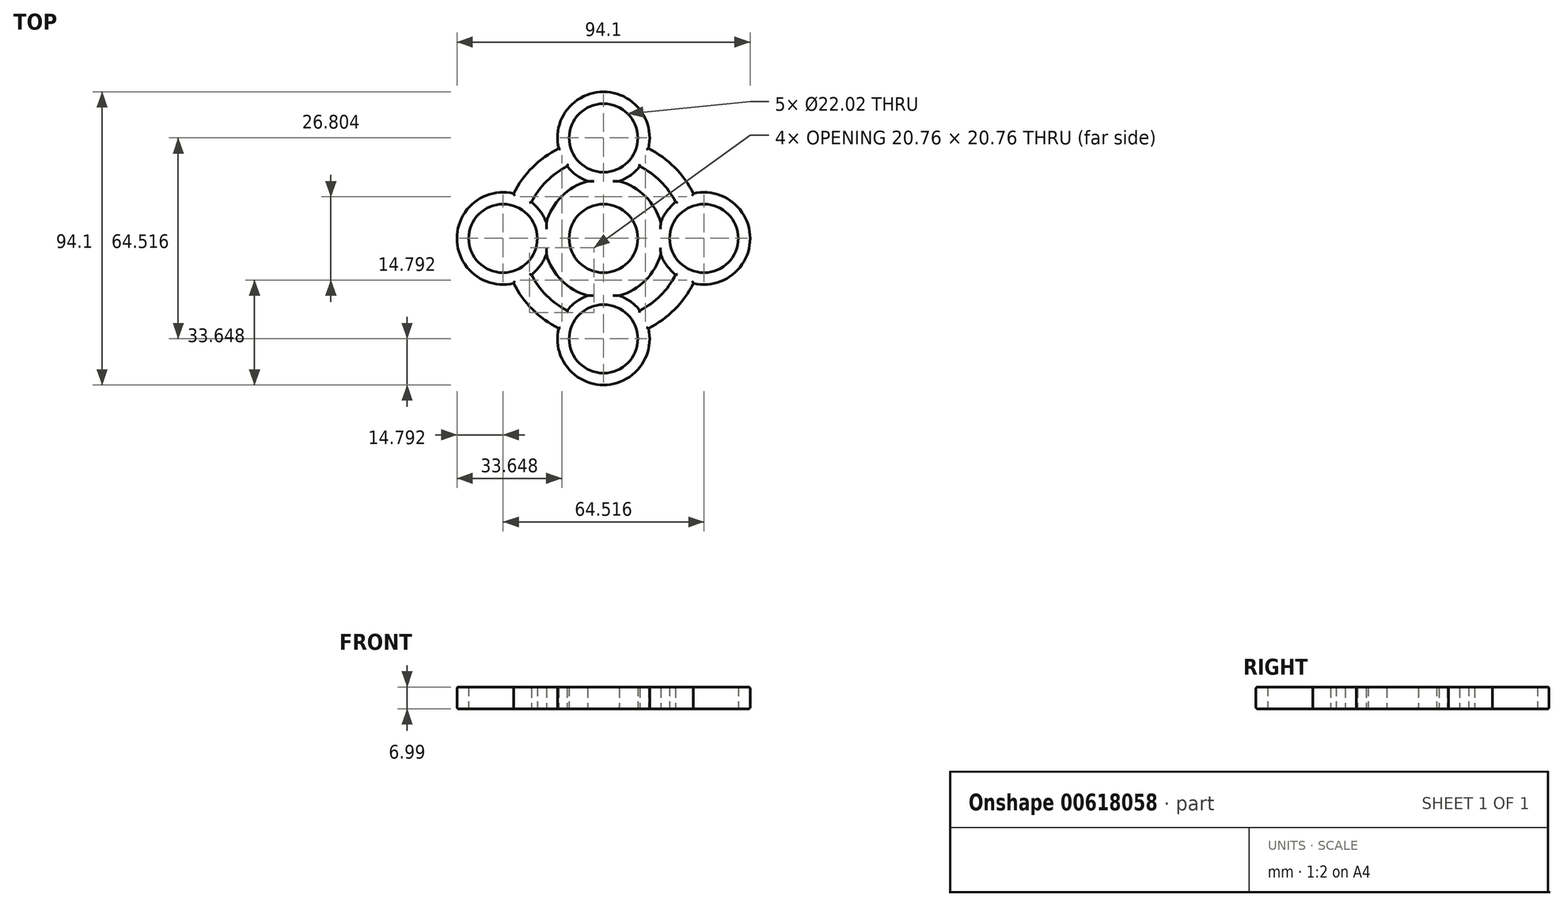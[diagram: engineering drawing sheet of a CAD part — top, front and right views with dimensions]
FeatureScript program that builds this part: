
annotation { "Feature Type Name" : "Feature", "Feature Type Description" : "" }
export const myFeature = defineFeature(function(context is Context, id is Id, definition is map)
    precondition{}
    {
        {
            var Q0;
            Q0=qCreatedBy(makeId("Top.planeOp"),FACE);
            var sketch = newSketch(context, id + "F0", { "sketchPlane" : qUnion([Q0])});
            skCircle(sketch, "E0", {"center": v(0, 0) * mm, "radius": 11.01 * mm});
            skCircle(sketch, "E1", {"center": v(-32.26, 0) * mm, "radius": 11.01 * mm});
            skCircle(sketch, "E2", {"center": v(0, 32.26) * mm, "radius": 11.01 * mm});
            skCircle(sketch, "E3", {"center": v(0, -32.26) * mm, "radius": 11.01 * mm});
            skCircle(sketch, "E4", {"center": v(32.26, 0) * mm, "radius": 11.01 * mm});
            skCircle(sketch, "E5", {"center": v(0, 32.26) * mm, "radius": 14.8 * mm});
            skCircle(sketch, "E6", {"center": v(-32.26, 0) * mm, "radius": 14.8 * mm});
            skCircle(sketch, "E7", {"center": v(0, -32.26) * mm, "radius": 14.8 * mm});
            skCircle(sketch, "E8", {"center": v(32.26, 0) * mm, "radius": 14.8 * mm});
            skLineSegment(sketch, "E9", {"start": v(-32.26, 0) * mm, "end": v(0, 0) * mm});
            skLineSegment(sketch, "E10", {"start": v(0, 0) * mm, "end": v(0, 32.26) * mm});
            skLineSegment(sketch, "E11", {"start": v(32.26, 0) * mm, "end": v(0, 0) * mm});
            skLineSegment(sketch, "E12", {"start": v(0, 0) * mm, "end": v(0, -32.26) * mm});
            skArc(sketch, "E13", {"start": v(-28.86, -14.4) * mm, "mid": v(-22.8, -22.8) * mm, "end": v(-14.4, -28.86) * mm});
            skArc(sketch, "E14.trimOffspring", {"start": v(-14.4, 28.86) * mm, "mid": v(-22.8, 22.8) * mm, "end": v(-28.86, 14.4) * mm});
            skArc(sketch, "E15.trimOffspring", {"start": v(28.86, 14.4) * mm, "mid": v(22.8, 22.8) * mm, "end": v(14.4, 28.86) * mm});
            skArc(sketch, "E16.trimOffspring", {"start": v(14.4, -28.86) * mm, "mid": v(22.8, -22.8) * mm, "end": v(28.86, -14.4) * mm});
            skArc(sketch, "E17", {"start": v(-23.14, -11.65) * mm, "mid": v(-18.32, -18.32) * mm, "end": v(-11.65, -23.14) * mm});
            skArc(sketch, "E18.trimOffspring", {"start": v(-11.65, 23.14) * mm, "mid": v(-18.32, 18.32) * mm, "end": v(-23.14, 11.65) * mm});
            skArc(sketch, "E19.trimOffspring", {"start": v(23.14, 11.65) * mm, "mid": v(18.32, 18.32) * mm, "end": v(11.65, 23.14) * mm});
            skArc(sketch, "E20.trimOffspring", {"start": v(11.65, -23.14) * mm, "mid": v(18.32, -18.32) * mm, "end": v(23.14, -11.65) * mm});
            skCircle(sketch, "E21", {"center": v(0, 0) * mm, "radius": 19.05 * mm});
            skSolve(sketch);
        }
        {
            var Q0;
            {var subQ0=sQuery(id+"F0.wireOp",EDGE,"E14.trimOffspring");Q0=makeQuery(id+"F0.imprint","IMPRINT",FACE,{"disambiguationData":[TD([[makeQuery(id+"F0.imprint","IMPRINT",EDGE,{"derivedFrom":subQ0}),1.0]])]});}
            var Q1;
            Q1=makeQuery(id+"F0.imprint","IMPRINT",FACE,{"disambiguationData":[TD([[makeQuery(id+"F0.imprint","IMPRINT",EDGE,{"derivedFrom":sQuery(id+"F0.wireOp",EDGE,"E1")}),-1.0]])]});
            var Q2;
            Q2=makeQuery(id+"F0.imprint","IMPRINT",FACE,{"disambiguationData":[TD([[makeQuery(id+"F0.imprint","IMPRINT",EDGE,{"derivedFrom":sQuery(id+"F0.wireOp",EDGE,"E2")}),-1.0]])]});
            var Q3;
            {var subQ0=sQuery(id+"F0.wireOp",EDGE,"E15.trimOffspring");Q3=makeQuery(id+"F0.imprint","IMPRINT",FACE,{"disambiguationData":[TD([[makeQuery(id+"F0.imprint","IMPRINT",EDGE,{"derivedFrom":subQ0}),1.0]])]});}
            var Q4;
            Q4=makeQuery(id+"F0.imprint","IMPRINT",FACE,{"disambiguationData":[TD([[makeQuery(id+"F0.imprint","IMPRINT",EDGE,{"derivedFrom":sQuery(id+"F0.wireOp",EDGE,"E4")}),-1.0]])]});
            var Q5;
            {var subQ0=sQuery(id+"F0.wireOp",EDGE,"E16.trimOffspring");Q5=makeQuery(id+"F0.imprint","IMPRINT",FACE,{"disambiguationData":[TD([[makeQuery(id+"F0.imprint","IMPRINT",EDGE,{"derivedFrom":subQ0}),1.0]])]});}
            var Q6;
            Q6=makeQuery(id+"F0.imprint","IMPRINT",FACE,{"disambiguationData":[TD([[makeQuery(id+"F0.imprint","IMPRINT",EDGE,{"derivedFrom":sQuery(id+"F0.wireOp",EDGE,"E3")}),-1.0]])]});
            var Q7;
            {var subQ0=sQuery(id+"F0.wireOp",EDGE,"E13");Q7=makeQuery(id+"F0.imprint","IMPRINT",FACE,{"disambiguationData":[TD([[makeQuery(id+"F0.imprint","IMPRINT",EDGE,{"derivedFrom":subQ0}),1.0]])]});}
            var Q8;
            {var subQ5=sQuery(id+"F0.wireOp",EDGE,"E9");var subQ9=sQuery(id+"F0.wireOp",EDGE,"E0");var subQ10=makeQuery(id+"F0.imprint","INTERSECT",VERTEX,{"derivedFrom":[subQ9,subQ5]});Q8=makeQuery(id+"F0.imprint","IMPRINT",FACE,{"disambiguationData":[TD([[makeQuery(id+"F0.imprint","IMPRINT",EDGE,{"disambiguationData":[TD([[subQ10,-1.0]])],"derivedFrom":subQ9}),-1.0]])]});}
            var Q9;
            {var subQ1=sQuery(id+"F0.wireOp",EDGE,"E0");var subQ9=sQuery(id+"F0.wireOp",EDGE,"E10");var subQ11=makeQuery(id+"F0.imprint","INTERSECT",VERTEX,{"derivedFrom":[subQ1,subQ9]});Q9=makeQuery(id+"F0.imprint","IMPRINT",FACE,{"disambiguationData":[TD([[makeQuery(id+"F0.imprint","IMPRINT",EDGE,{"disambiguationData":[TD([[subQ11,-1.0]])],"derivedFrom":subQ1}),-1.0]])]});}
            var Q10;
            {var subQ5=sQuery(id+"F0.wireOp",EDGE,"E10");var subQ9=sQuery(id+"F0.wireOp",EDGE,"E0");var subQ10=makeQuery(id+"F0.imprint","INTERSECT",VERTEX,{"derivedFrom":[subQ9,subQ5]});Q10=makeQuery(id+"F0.imprint","IMPRINT",FACE,{"disambiguationData":[TD([[makeQuery(id+"F0.imprint","IMPRINT",EDGE,{"disambiguationData":[TD([[subQ10,1.0]])],"derivedFrom":subQ9}),-1.0]])]});}
            var Q11;
            {var subQ0=sQuery(id+"F0.wireOp",EDGE,"E11");var subQ5=sQuery(id+"F0.wireOp",EDGE,"E0");var subQ6=makeQuery(id+"F0.imprint","INTERSECT",VERTEX,{"derivedFrom":[subQ5,subQ0]});Q11=makeQuery(id+"F0.imprint","IMPRINT",FACE,{"disambiguationData":[TD([[makeQuery(id+"F0.imprint","IMPRINT",EDGE,{"disambiguationData":[TD([[subQ6,1.0]])],"derivedFrom":subQ5}),-1.0]])]});}
            var Q12;
            {var subQ0=sQuery(id+"F0.wireOp",EDGE,"E21");var subQ1=sQuery(id+"F0.wireOp",EDGE,"E8");var subQ2=makeQuery(id+"F0.imprint","INTERSECT",VERTEX,{"disambiguationData":[OD(0.0)],"derivedFrom":[subQ1,subQ0]});Q12=makeQuery(id+"F0.imprint","IMPRINT",FACE,{"disambiguationData":[TD([[makeQuery(id+"F0.imprint","IMPRINT",EDGE,{"disambiguationData":[TD([[subQ2,-1.0]])],"derivedFrom":subQ1}),1.0]])]});}
            var Q13;
            {var subQ0=sQuery(id+"F0.wireOp",EDGE,"E11");var subQ1=sQuery(id+"F0.wireOp",EDGE,"E8");var subQ2=makeQuery(id+"F0.imprint","INTERSECT",VERTEX,{"derivedFrom":[subQ1,subQ0]});Q13=makeQuery(id+"F0.imprint","IMPRINT",FACE,{"disambiguationData":[TD([[makeQuery(id+"F0.imprint","IMPRINT",EDGE,{"disambiguationData":[TD([[subQ2,-1.0]])],"derivedFrom":subQ1}),1.0]])]});}
            var Q14;
            {var subQ0=sQuery(id+"F0.wireOp",EDGE,"E10");var subQ1=sQuery(id+"F0.wireOp",EDGE,"E5");var subQ2=makeQuery(id+"F0.imprint","INTERSECT",VERTEX,{"derivedFrom":[subQ1,subQ0]});Q14=makeQuery(id+"F0.imprint","IMPRINT",FACE,{"disambiguationData":[TD([[makeQuery(id+"F0.imprint","IMPRINT",EDGE,{"disambiguationData":[TD([[subQ2,-1.0]])],"derivedFrom":subQ1}),1.0]])]});}
            var Q15;
            {var subQ0=sQuery(id+"F0.wireOp",EDGE,"E21");var subQ1=sQuery(id+"F0.wireOp",EDGE,"E5");var subQ2=makeQuery(id+"F0.imprint","INTERSECT",VERTEX,{"disambiguationData":[OD(0.0)],"derivedFrom":[subQ1,subQ0]});Q15=makeQuery(id+"F0.imprint","IMPRINT",FACE,{"disambiguationData":[TD([[makeQuery(id+"F0.imprint","IMPRINT",EDGE,{"disambiguationData":[TD([[subQ2,-1.0]])],"derivedFrom":subQ1}),1.0]])]});}
            var Q16;
            {var subQ0=sQuery(id+"F0.wireOp",EDGE,"E9");var subQ1=sQuery(id+"F0.wireOp",EDGE,"E6");var subQ2=makeQuery(id+"F0.imprint","INTERSECT",VERTEX,{"derivedFrom":[subQ1,subQ0]});Q16=makeQuery(id+"F0.imprint","IMPRINT",FACE,{"disambiguationData":[TD([[makeQuery(id+"F0.imprint","IMPRINT",EDGE,{"disambiguationData":[TD([[subQ2,1.0]])],"derivedFrom":subQ1}),1.0]])]});}
            var Q17;
            {var subQ0=sQuery(id+"F0.wireOp",EDGE,"E21");var subQ1=sQuery(id+"F0.wireOp",EDGE,"E6");var subQ2=makeQuery(id+"F0.imprint","INTERSECT",VERTEX,{"disambiguationData":[OD(0.0)],"derivedFrom":[subQ1,subQ0]});Q17=makeQuery(id+"F0.imprint","IMPRINT",FACE,{"disambiguationData":[TD([[makeQuery(id+"F0.imprint","IMPRINT",EDGE,{"disambiguationData":[TD([[subQ2,1.0]])],"derivedFrom":subQ1}),1.0]])]});}
            var Q18;
            {var subQ0=sQuery(id+"F0.wireOp",EDGE,"E21");var subQ1=sQuery(id+"F0.wireOp",EDGE,"E7");var subQ2=makeQuery(id+"F0.imprint","INTERSECT",VERTEX,{"disambiguationData":[OD(0.0)],"derivedFrom":[subQ1,subQ0]});Q18=makeQuery(id+"F0.imprint","IMPRINT",FACE,{"disambiguationData":[TD([[makeQuery(id+"F0.imprint","IMPRINT",EDGE,{"disambiguationData":[TD([[subQ2,-1.0]])],"derivedFrom":subQ1}),1.0]])]});}
            var Q19;
            {var subQ0=sQuery(id+"F0.wireOp",EDGE,"E12");var subQ1=sQuery(id+"F0.wireOp",EDGE,"E7");var subQ2=makeQuery(id+"F0.imprint","INTERSECT",VERTEX,{"derivedFrom":[subQ1,subQ0]});Q19=makeQuery(id+"F0.imprint","IMPRINT",FACE,{"disambiguationData":[TD([[makeQuery(id+"F0.imprint","IMPRINT",EDGE,{"disambiguationData":[TD([[subQ2,-1.0]])],"derivedFrom":subQ1}),1.0]])]});}
            extrude(context, id + "F1", {"entities" : qUnion([Q0, Q1, Q2, Q3, Q4, Q5, Q6, Q7, Q8, Q9, Q10, Q11, Q12, Q13, Q14, Q15, Q16, Q17, Q18, Q19]), "depth" : 7 * mm, "offsetDistance" : 25.4 * mm});
        }
        {
            var Q0;
            Q0=makeQuery(id+"F1.opExtrude","CAP_EDGE",EDGE,{"disambiguationData":[OSD([sQuery(id+"F0.wireOp",EDGE,"E14.trimOffspring")])],"isStart":false});
            var Q1;
            {var subQ0=sQuery(id+"F0.wireOp",EDGE,"E5");Q1=makeQuery(id+"F1.opExtrude","CAP_EDGE",EDGE,{"disambiguationData":[OSD([subQ0]),TDD([makeQuery(id+"F0.imprint","IMPRINT",EDGE,{"disambiguationData":[TD([[makeQuery(id+"F0.imprint","INTERSECT",VERTEX,{"derivedFrom":[subQ0,sQuery(id+"F0.wireOp",EDGE,"E14.trimOffspring")]}),1.0]])],"derivedFrom":subQ0})])],"isStart":false});}
            var Q2;
            {var subQ0=sQuery(id+"F0.wireOp",EDGE,"E6");Q2=makeQuery(id+"F1.opExtrude","CAP_EDGE",EDGE,{"disambiguationData":[OSD([subQ0]),TDD([makeQuery(id+"F0.imprint","IMPRINT",EDGE,{"disambiguationData":[TD([[makeQuery(id+"F0.imprint","INTERSECT",VERTEX,{"derivedFrom":[subQ0,sQuery(id+"F0.wireOp",EDGE,"E13")]}),1.0]])],"derivedFrom":subQ0})])],"isStart":false});}
            var Q3;
            Q3=makeQuery(id+"F1.opExtrude","CAP_EDGE",EDGE,{"disambiguationData":[OSD([sQuery(id+"F0.wireOp",EDGE,"E13")])],"isStart":false});
            var Q4;
            {var subQ0=sQuery(id+"F0.wireOp",EDGE,"E7");Q4=makeQuery(id+"F1.opExtrude","CAP_EDGE",EDGE,{"disambiguationData":[OSD([subQ0]),TDD([makeQuery(id+"F0.imprint","IMPRINT",EDGE,{"disambiguationData":[TD([[makeQuery(id+"F0.imprint","INTERSECT",VERTEX,{"derivedFrom":[subQ0,sQuery(id+"F0.wireOp",EDGE,"E13")]}),-1.0]])],"derivedFrom":subQ0})])],"isStart":false});}
            var Q5;
            Q5=makeQuery(id+"F1.opExtrude","CAP_EDGE",EDGE,{"disambiguationData":[OSD([sQuery(id+"F0.wireOp",EDGE,"E16.trimOffspring")])],"isStart":false});
            var Q6;
            {var subQ0=sQuery(id+"F0.wireOp",EDGE,"E8");Q6=makeQuery(id+"F1.opExtrude","CAP_EDGE",EDGE,{"disambiguationData":[OSD([subQ0]),TDD([makeQuery(id+"F0.imprint","IMPRINT",EDGE,{"disambiguationData":[TD([[makeQuery(id+"F0.imprint","INTERSECT",VERTEX,{"derivedFrom":[subQ0,sQuery(id+"F0.wireOp",EDGE,"E15.trimOffspring")]}),1.0]])],"derivedFrom":subQ0})])],"isStart":false});}
            var Q7;
            Q7=makeQuery(id+"F1.opExtrude","CAP_EDGE",EDGE,{"disambiguationData":[OSD([sQuery(id+"F0.wireOp",EDGE,"E15.trimOffspring")])],"isStart":false});
            fillet(context, id + "F2", {"entities" : qUnion([Q0, Q1, Q2, Q3, Q4, Q5, Q6, Q7]), "radius" : 0.5 * mm, "tangentPropagation" : true, "allowEdgeOverflow" : false});
        }
        {
            var Q0;
            Q0=makeQuery(id+"F1.opExtrude","CAP_EDGE",EDGE,{"disambiguationData":[OSD([sQuery(id+"F0.wireOp",EDGE,"E14.trimOffspring")])],"isStart":true});
            var Q1;
            {var subQ0=sQuery(id+"F0.wireOp",EDGE,"E6");Q1=makeQuery(id+"F1.opExtrude","CAP_EDGE",EDGE,{"disambiguationData":[OSD([subQ0]),TDD([makeQuery(id+"F0.imprint","IMPRINT",EDGE,{"disambiguationData":[TD([[makeQuery(id+"F0.imprint","INTERSECT",VERTEX,{"derivedFrom":[subQ0,sQuery(id+"F0.wireOp",EDGE,"E13")]}),1.0]])],"derivedFrom":subQ0})])],"isStart":true});}
            var Q2;
            Q2=makeQuery(id+"F1.opExtrude","CAP_EDGE",EDGE,{"disambiguationData":[OSD([sQuery(id+"F0.wireOp",EDGE,"E13")])],"isStart":true});
            var Q3;
            {var subQ0=sQuery(id+"F0.wireOp",EDGE,"E7");Q3=makeQuery(id+"F1.opExtrude","CAP_EDGE",EDGE,{"disambiguationData":[OSD([subQ0]),TDD([makeQuery(id+"F0.imprint","IMPRINT",EDGE,{"disambiguationData":[TD([[makeQuery(id+"F0.imprint","INTERSECT",VERTEX,{"derivedFrom":[subQ0,sQuery(id+"F0.wireOp",EDGE,"E13")]}),-1.0]])],"derivedFrom":subQ0})])],"isStart":true});}
            var Q4;
            Q4=makeQuery(id+"F1.opExtrude","CAP_EDGE",EDGE,{"disambiguationData":[OSD([sQuery(id+"F0.wireOp",EDGE,"E16.trimOffspring")])],"isStart":true});
            var Q5;
            {var subQ0=sQuery(id+"F0.wireOp",EDGE,"E8");Q5=makeQuery(id+"F1.opExtrude","CAP_EDGE",EDGE,{"disambiguationData":[OSD([subQ0]),TDD([makeQuery(id+"F0.imprint","IMPRINT",EDGE,{"disambiguationData":[TD([[makeQuery(id+"F0.imprint","INTERSECT",VERTEX,{"derivedFrom":[subQ0,sQuery(id+"F0.wireOp",EDGE,"E15.trimOffspring")]}),1.0]])],"derivedFrom":subQ0})])],"isStart":true});}
            var Q6;
            Q6=makeQuery(id+"F1.opExtrude","CAP_EDGE",EDGE,{"disambiguationData":[OSD([sQuery(id+"F0.wireOp",EDGE,"E15.trimOffspring")])],"isStart":true});
            var Q7;
            {var subQ0=sQuery(id+"F0.wireOp",EDGE,"E5");Q7=makeQuery(id+"F1.opExtrude","CAP_EDGE",EDGE,{"disambiguationData":[OSD([subQ0]),TDD([makeQuery(id+"F0.imprint","IMPRINT",EDGE,{"disambiguationData":[TD([[makeQuery(id+"F0.imprint","INTERSECT",VERTEX,{"derivedFrom":[subQ0,sQuery(id+"F0.wireOp",EDGE,"E14.trimOffspring")]}),1.0]])],"derivedFrom":subQ0})])],"isStart":true});}
            fillet(context, id + "F3", {"entities" : qUnion([Q0, Q1, Q2, Q3, Q4, Q5, Q6, Q7]), "radius" : 0.5 * mm, "tangentPropagation" : true, "allowEdgeOverflow" : false});
        }
        {
            var Q0;
            {var subQ0=sQuery(id+"F0.wireOp",EDGE,"E21");Q0=makeQuery(id+"F1.opExtrude","CAP_EDGE",EDGE,{"disambiguationData":[OSD([subQ0]),TDD([makeQuery(id+"F0.imprint","IMPRINT",EDGE,{"disambiguationData":[TD([[makeQuery(id+"F0.imprint","INTERSECT",VERTEX,{"disambiguationData":[OD(1.0)],"derivedFrom":[sQuery(id+"F0.wireOp",EDGE,"E6"),subQ0]}),-1.0]])],"derivedFrom":subQ0})])],"isStart":false});}
            var Q1;
            {var subQ0=sQuery(id+"F0.wireOp",EDGE,"E21");Q1=makeQuery(id+"F1.opExtrude","CAP_EDGE",EDGE,{"disambiguationData":[OSD([subQ0]),TDD([makeQuery(id+"F0.imprint","IMPRINT",EDGE,{"disambiguationData":[TD([[makeQuery(id+"F0.imprint","INTERSECT",VERTEX,{"disambiguationData":[OD(0.0)],"derivedFrom":[sQuery(id+"F0.wireOp",EDGE,"E7"),subQ0]}),-1.0]])],"derivedFrom":subQ0})])],"isStart":false});}
            var Q2;
            {var subQ0=sQuery(id+"F0.wireOp",EDGE,"E21");Q2=makeQuery(id+"F1.opExtrude","CAP_EDGE",EDGE,{"disambiguationData":[OSD([subQ0]),TDD([makeQuery(id+"F0.imprint","IMPRINT",EDGE,{"disambiguationData":[TD([[makeQuery(id+"F0.imprint","INTERSECT",VERTEX,{"disambiguationData":[OD(1.0)],"derivedFrom":[sQuery(id+"F0.wireOp",EDGE,"E5"),subQ0]}),1.0]])],"derivedFrom":subQ0})])],"isStart":false});}
            var Q3;
            {var subQ0=sQuery(id+"F0.wireOp",EDGE,"E21");Q3=makeQuery(id+"F1.opExtrude","CAP_EDGE",EDGE,{"disambiguationData":[OSD([subQ0]),TDD([makeQuery(id+"F0.imprint","IMPRINT",EDGE,{"disambiguationData":[TD([[makeQuery(id+"F0.imprint","INTERSECT",VERTEX,{"disambiguationData":[OD(0.0)],"derivedFrom":[sQuery(id+"F0.wireOp",EDGE,"E5"),subQ0]}),-1.0]])],"derivedFrom":subQ0})])],"isStart":false});}
            var Q4;
            Q4=makeQuery(id+"F1.opExtrude","CAP_EDGE",EDGE,{"disambiguationData":[OSD([sQuery(id+"F0.wireOp",EDGE,"E17")])],"isStart":false});
            var Q5;
            Q5=makeQuery(id+"F1.opExtrude","CAP_EDGE",EDGE,{"disambiguationData":[OSD([sQuery(id+"F0.wireOp",EDGE,"E18.trimOffspring")])],"isStart":false});
            var Q6;
            Q6=makeQuery(id+"F1.opExtrude","CAP_EDGE",EDGE,{"disambiguationData":[OSD([sQuery(id+"F0.wireOp",EDGE,"E19.trimOffspring")])],"isStart":false});
            var Q7;
            Q7=makeQuery(id+"F1.opExtrude","CAP_EDGE",EDGE,{"disambiguationData":[OSD([sQuery(id+"F0.wireOp",EDGE,"E20.trimOffspring")])],"isStart":false});
            fillet(context, id + "F4", {"entities" : qUnion([Q0, Q1, Q2, Q3, Q4, Q5, Q6, Q7]), "radius" : 0.5 * mm, "tangentPropagation" : true, "allowEdgeOverflow" : false});
        }
        {
            var Q0;
            Q0=makeQuery(id+"F1.opExtrude","CAP_EDGE",EDGE,{"disambiguationData":[OSD([sQuery(id+"F0.wireOp",EDGE,"E19.trimOffspring")])],"isStart":true});
            var Q1;
            {var subQ0=sQuery(id+"F0.wireOp",EDGE,"E21");Q1=makeQuery(id+"F1.opExtrude","CAP_EDGE",EDGE,{"disambiguationData":[OSD([subQ0]),TDD([makeQuery(id+"F0.imprint","IMPRINT",EDGE,{"disambiguationData":[TD([[makeQuery(id+"F0.imprint","INTERSECT",VERTEX,{"disambiguationData":[OD(1.0)],"derivedFrom":[sQuery(id+"F0.wireOp",EDGE,"E5"),subQ0]}),1.0]])],"derivedFrom":subQ0})])],"isStart":true});}
            var Q2;
            Q2=makeQuery(id+"F1.opExtrude","CAP_EDGE",EDGE,{"disambiguationData":[OSD([sQuery(id+"F0.wireOp",EDGE,"E18.trimOffspring")])],"isStart":true});
            var Q3;
            {var subQ0=sQuery(id+"F0.wireOp",EDGE,"E21");Q3=makeQuery(id+"F1.opExtrude","CAP_EDGE",EDGE,{"disambiguationData":[OSD([subQ0]),TDD([makeQuery(id+"F0.imprint","IMPRINT",EDGE,{"disambiguationData":[TD([[makeQuery(id+"F0.imprint","INTERSECT",VERTEX,{"disambiguationData":[OD(0.0)],"derivedFrom":[sQuery(id+"F0.wireOp",EDGE,"E5"),subQ0]}),-1.0]])],"derivedFrom":subQ0})])],"isStart":true});}
            var Q4;
            {var subQ0=sQuery(id+"F0.wireOp",EDGE,"E21");Q4=makeQuery(id+"F1.opExtrude","CAP_EDGE",EDGE,{"disambiguationData":[OSD([subQ0]),TDD([makeQuery(id+"F0.imprint","IMPRINT",EDGE,{"disambiguationData":[TD([[makeQuery(id+"F0.imprint","INTERSECT",VERTEX,{"disambiguationData":[OD(1.0)],"derivedFrom":[sQuery(id+"F0.wireOp",EDGE,"E6"),subQ0]}),-1.0]])],"derivedFrom":subQ0})])],"isStart":true});}
            var Q5;
            Q5=makeQuery(id+"F1.opExtrude","CAP_EDGE",EDGE,{"disambiguationData":[OSD([sQuery(id+"F0.wireOp",EDGE,"E17")])],"isStart":true});
            var Q6;
            Q6=makeQuery(id+"F1.opExtrude","CAP_EDGE",EDGE,{"disambiguationData":[OSD([sQuery(id+"F0.wireOp",EDGE,"E20.trimOffspring")])],"isStart":true});
            var Q7;
            {var subQ0=sQuery(id+"F0.wireOp",EDGE,"E21");Q7=makeQuery(id+"F1.opExtrude","CAP_EDGE",EDGE,{"disambiguationData":[OSD([subQ0]),TDD([makeQuery(id+"F0.imprint","IMPRINT",EDGE,{"disambiguationData":[TD([[makeQuery(id+"F0.imprint","INTERSECT",VERTEX,{"disambiguationData":[OD(0.0)],"derivedFrom":[sQuery(id+"F0.wireOp",EDGE,"E7"),subQ0]}),-1.0]])],"derivedFrom":subQ0})])],"isStart":true});}
            fillet(context, id + "F5", {"entities" : qUnion([Q0, Q1, Q2, Q3, Q4, Q5, Q6, Q7]), "radius" : 0.5 * mm, "tangentPropagation" : true, "allowEdgeOverflow" : false});
        }
        {
            var Q0;
            {var subQ0=sQuery(id+"F0.wireOp",EDGE,"E5");Q0=makeQuery(id+"F1.opExtrude","CAP_EDGE",EDGE,{"disambiguationData":[OSD([subQ0]),TDD([makeQuery(id+"F0.imprint","IMPRINT",EDGE,{"disambiguationData":[TD([[makeQuery(id+"F0.imprint","INTERSECT",VERTEX,{"derivedFrom":[subQ0,sQuery(id+"F0.wireOp",EDGE,"E19.trimOffspring")]}),1.0]])],"derivedFrom":subQ0})])],"isStart":true});}
            var Q1;
            {var subQ0=sQuery(id+"F0.wireOp",EDGE,"E5");Q1=makeQuery(id+"F1.opExtrude","CAP_EDGE",EDGE,{"disambiguationData":[OSD([subQ0]),TDD([makeQuery(id+"F0.imprint","IMPRINT",EDGE,{"disambiguationData":[TD([[makeQuery(id+"F0.imprint","INTERSECT",VERTEX,{"derivedFrom":[subQ0,sQuery(id+"F0.wireOp",EDGE,"E18.trimOffspring")]}),-1.0]])],"derivedFrom":subQ0})])],"isStart":true});}
            var Q2;
            {var subQ0=sQuery(id+"F0.wireOp",EDGE,"E6");Q2=makeQuery(id+"F1.opExtrude","CAP_EDGE",EDGE,{"disambiguationData":[OSD([subQ0]),TDD([makeQuery(id+"F0.imprint","IMPRINT",EDGE,{"disambiguationData":[TD([[makeQuery(id+"F0.imprint","INTERSECT",VERTEX,{"derivedFrom":[subQ0,sQuery(id+"F0.wireOp",EDGE,"E18.trimOffspring")]}),1.0]])],"derivedFrom":subQ0})])],"isStart":true});}
            var Q3;
            {var subQ0=sQuery(id+"F0.wireOp",EDGE,"E6");Q3=makeQuery(id+"F1.opExtrude","CAP_EDGE",EDGE,{"disambiguationData":[OSD([subQ0]),TDD([makeQuery(id+"F0.imprint","IMPRINT",EDGE,{"disambiguationData":[TD([[makeQuery(id+"F0.imprint","INTERSECT",VERTEX,{"derivedFrom":[subQ0,sQuery(id+"F0.wireOp",EDGE,"E17")]}),-1.0]])],"derivedFrom":subQ0})])],"isStart":true});}
            var Q4;
            {var subQ0=sQuery(id+"F0.wireOp",EDGE,"E7");Q4=makeQuery(id+"F1.opExtrude","CAP_EDGE",EDGE,{"disambiguationData":[OSD([subQ0]),TDD([makeQuery(id+"F0.imprint","IMPRINT",EDGE,{"disambiguationData":[TD([[makeQuery(id+"F0.imprint","INTERSECT",VERTEX,{"derivedFrom":[subQ0,sQuery(id+"F0.wireOp",EDGE,"E17")]}),1.0]])],"derivedFrom":subQ0})])],"isStart":true});}
            var Q5;
            {var subQ0=sQuery(id+"F0.wireOp",EDGE,"E7");Q5=makeQuery(id+"F1.opExtrude","CAP_EDGE",EDGE,{"disambiguationData":[OSD([subQ0]),TDD([makeQuery(id+"F0.imprint","IMPRINT",EDGE,{"disambiguationData":[TD([[makeQuery(id+"F0.imprint","INTERSECT",VERTEX,{"derivedFrom":[subQ0,sQuery(id+"F0.wireOp",EDGE,"E20.trimOffspring")]}),-1.0]])],"derivedFrom":subQ0})])],"isStart":true});}
            var Q6;
            {var subQ0=sQuery(id+"F0.wireOp",EDGE,"E8");Q6=makeQuery(id+"F1.opExtrude","CAP_EDGE",EDGE,{"disambiguationData":[OSD([subQ0]),TDD([makeQuery(id+"F0.imprint","IMPRINT",EDGE,{"disambiguationData":[TD([[makeQuery(id+"F0.imprint","INTERSECT",VERTEX,{"derivedFrom":[subQ0,sQuery(id+"F0.wireOp",EDGE,"E20.trimOffspring")]}),1.0]])],"derivedFrom":subQ0})])],"isStart":true});}
            var Q7;
            {var subQ0=sQuery(id+"F0.wireOp",EDGE,"E8");Q7=makeQuery(id+"F1.opExtrude","CAP_EDGE",EDGE,{"disambiguationData":[OSD([subQ0]),TDD([makeQuery(id+"F0.imprint","IMPRINT",EDGE,{"disambiguationData":[TD([[makeQuery(id+"F0.imprint","INTERSECT",VERTEX,{"derivedFrom":[subQ0,sQuery(id+"F0.wireOp",EDGE,"E19.trimOffspring")]}),-1.0]])],"derivedFrom":subQ0})])],"isStart":true});}
            fillet(context, id + "F6", {"entities" : qUnion([Q0, Q1, Q2, Q3, Q4, Q5, Q6, Q7]), "radius" : 0.5 * mm, "tangentPropagation" : true, "allowEdgeOverflow" : false});
        }
        {
            var Q0;
            {var subQ0=sQuery(id+"F0.wireOp",EDGE,"E6");Q0=makeQuery(id+"F1.opExtrude","CAP_EDGE",EDGE,{"disambiguationData":[OSD([subQ0]),TDD([makeQuery(id+"F0.imprint","IMPRINT",EDGE,{"disambiguationData":[TD([[makeQuery(id+"F0.imprint","INTERSECT",VERTEX,{"derivedFrom":[subQ0,sQuery(id+"F0.wireOp",EDGE,"E17")]}),-1.0]])],"derivedFrom":subQ0})])],"isStart":false});}
            var Q1;
            {var subQ0=sQuery(id+"F0.wireOp",EDGE,"E6");Q1=makeQuery(id+"F1.opExtrude","CAP_EDGE",EDGE,{"disambiguationData":[OSD([subQ0]),TDD([makeQuery(id+"F0.imprint","IMPRINT",EDGE,{"disambiguationData":[TD([[makeQuery(id+"F0.imprint","INTERSECT",VERTEX,{"derivedFrom":[subQ0,sQuery(id+"F0.wireOp",EDGE,"E18.trimOffspring")]}),1.0]])],"derivedFrom":subQ0})])],"isStart":false});}
            var Q2;
            {var subQ0=sQuery(id+"F0.wireOp",EDGE,"E5");Q2=makeQuery(id+"F1.opExtrude","CAP_EDGE",EDGE,{"disambiguationData":[OSD([subQ0]),TDD([makeQuery(id+"F0.imprint","IMPRINT",EDGE,{"disambiguationData":[TD([[makeQuery(id+"F0.imprint","INTERSECT",VERTEX,{"derivedFrom":[subQ0,sQuery(id+"F0.wireOp",EDGE,"E18.trimOffspring")]}),-1.0]])],"derivedFrom":subQ0})])],"isStart":false});}
            var Q3;
            {var subQ0=sQuery(id+"F0.wireOp",EDGE,"E5");Q3=makeQuery(id+"F1.opExtrude","CAP_EDGE",EDGE,{"disambiguationData":[OSD([subQ0]),TDD([makeQuery(id+"F0.imprint","IMPRINT",EDGE,{"disambiguationData":[TD([[makeQuery(id+"F0.imprint","INTERSECT",VERTEX,{"derivedFrom":[subQ0,sQuery(id+"F0.wireOp",EDGE,"E19.trimOffspring")]}),1.0]])],"derivedFrom":subQ0})])],"isStart":false});}
            var Q4;
            {var subQ0=sQuery(id+"F0.wireOp",EDGE,"E8");Q4=makeQuery(id+"F1.opExtrude","CAP_EDGE",EDGE,{"disambiguationData":[OSD([subQ0]),TDD([makeQuery(id+"F0.imprint","IMPRINT",EDGE,{"disambiguationData":[TD([[makeQuery(id+"F0.imprint","INTERSECT",VERTEX,{"derivedFrom":[subQ0,sQuery(id+"F0.wireOp",EDGE,"E19.trimOffspring")]}),-1.0]])],"derivedFrom":subQ0})])],"isStart":false});}
            var Q5;
            {var subQ0=sQuery(id+"F0.wireOp",EDGE,"E8");Q5=makeQuery(id+"F1.opExtrude","CAP_EDGE",EDGE,{"disambiguationData":[OSD([subQ0]),TDD([makeQuery(id+"F0.imprint","IMPRINT",EDGE,{"disambiguationData":[TD([[makeQuery(id+"F0.imprint","INTERSECT",VERTEX,{"derivedFrom":[subQ0,sQuery(id+"F0.wireOp",EDGE,"E20.trimOffspring")]}),1.0]])],"derivedFrom":subQ0})])],"isStart":false});}
            var Q6;
            {var subQ0=sQuery(id+"F0.wireOp",EDGE,"E7");Q6=makeQuery(id+"F1.opExtrude","CAP_EDGE",EDGE,{"disambiguationData":[OSD([subQ0]),TDD([makeQuery(id+"F0.imprint","IMPRINT",EDGE,{"disambiguationData":[TD([[makeQuery(id+"F0.imprint","INTERSECT",VERTEX,{"derivedFrom":[subQ0,sQuery(id+"F0.wireOp",EDGE,"E20.trimOffspring")]}),-1.0]])],"derivedFrom":subQ0})])],"isStart":false});}
            var Q7;
            {var subQ0=sQuery(id+"F0.wireOp",EDGE,"E7");Q7=makeQuery(id+"F1.opExtrude","CAP_EDGE",EDGE,{"disambiguationData":[OSD([subQ0]),TDD([makeQuery(id+"F0.imprint","IMPRINT",EDGE,{"disambiguationData":[TD([[makeQuery(id+"F0.imprint","INTERSECT",VERTEX,{"derivedFrom":[subQ0,sQuery(id+"F0.wireOp",EDGE,"E17")]}),1.0]])],"derivedFrom":subQ0})])],"isStart":false});}
            fillet(context, id + "F7", {"entities" : qUnion([Q0, Q1, Q2, Q3, Q4, Q5, Q6, Q7]), "radius" : 0.5 * mm, "tangentPropagation" : true, "allowEdgeOverflow" : false});
        }
    });
